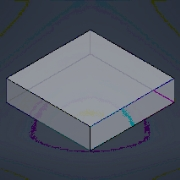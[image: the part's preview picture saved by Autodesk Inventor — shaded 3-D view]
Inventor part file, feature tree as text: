
AUTODESK INVENTOR PART (.ipt)
format: ipt  version: 2024.3 (Build 283343000, 343)  size: 130,560 bytes
history: native  units: mm
features: extrude x1, sketch x1
ambient origin geometry x8: Origin, YZ Plane, XZ Plane, XY Plane, X Axis, Y Axis, Z Axis, Center Point
bodies: Solid1 (feature_tree)
feature tree (2):
  extrude  "Extrusion1"  Depth=100.0mm
  sketch  "Sketch1"  dims[d0=100.0mm d1=100.0mm d2=100.0mm d3=0.0mm]
